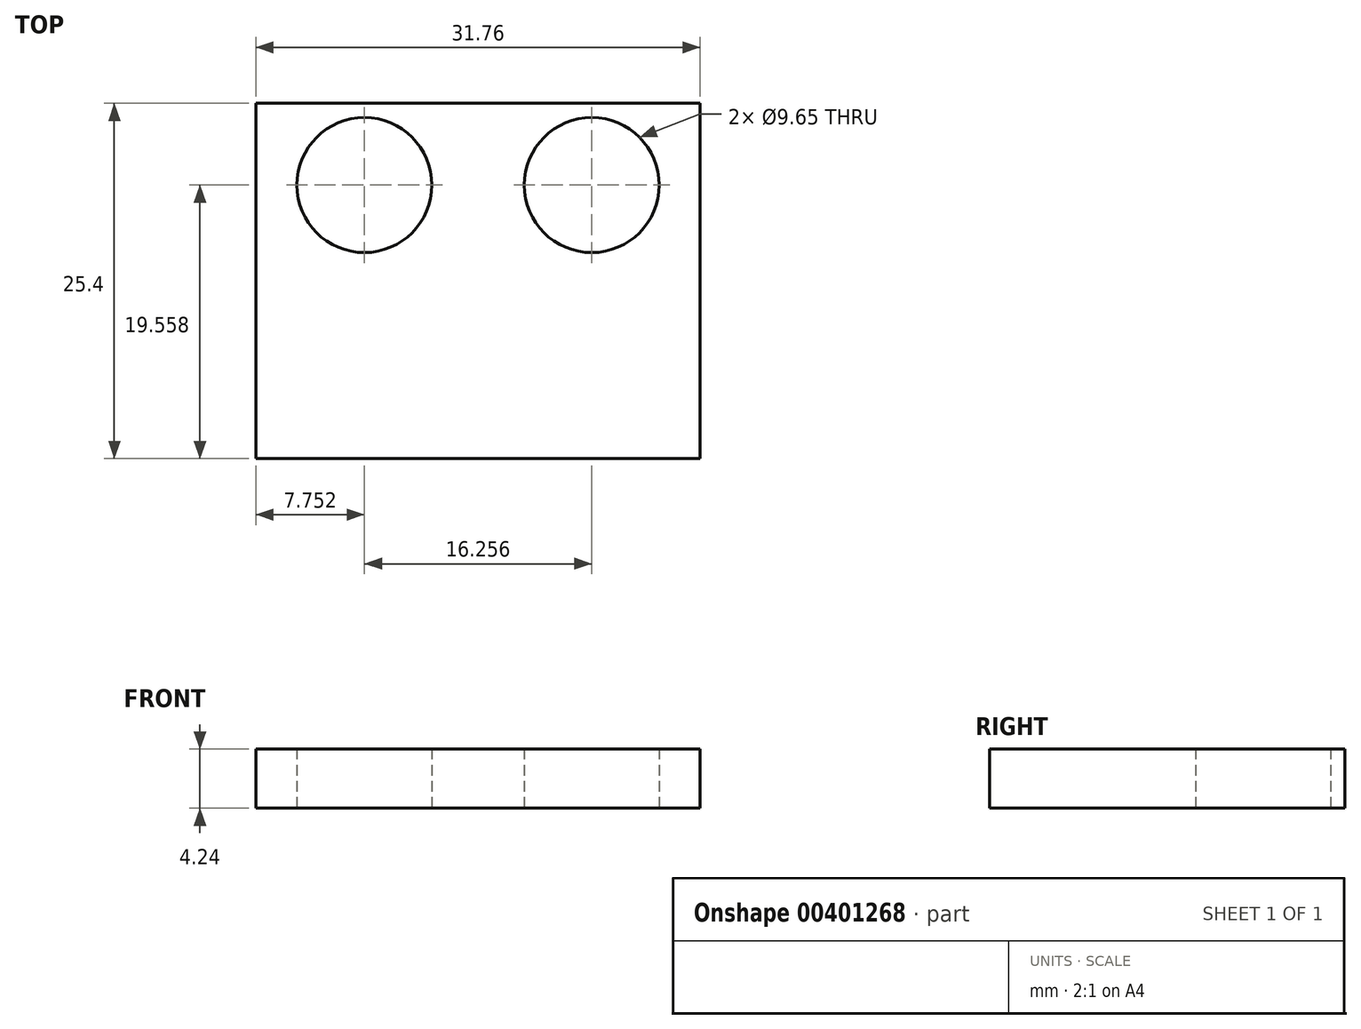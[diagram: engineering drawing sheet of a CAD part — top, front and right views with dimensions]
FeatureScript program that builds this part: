
annotation { "Feature Type Name" : "Feature", "Feature Type Description" : "" }
export const myFeature = defineFeature(function(context is Context, id is Id, definition is map)
    precondition{}
    {
        {
            var Q0;
            Q0=qCreatedBy(makeId("Top.planeOp"),FACE);
            var sketch = newSketch(context, id + "F0", { "sketchPlane" : qUnion([Q0])});
            skLineSegment(sketch, "E0.bottom", {"start": v(-15.87, -12.7) * mm, "end": v(15.88, -12.7) * mm});
            skLineSegment(sketch, "E0.top", {"start": v(-15.88, 12.7) * mm, "end": v(15.88, 12.7) * mm});
            skLineSegment(sketch, "E0.left", {"start": v(-15.87, -12.7) * mm, "end": v(-15.88, 12.7) * mm});
            skLineSegment(sketch, "E0.right", {"start": v(15.88, -12.7) * mm, "end": v(15.87, 12.7) * mm});
            skPoint(sketch, "E0.middle", {"position": v(0, 0) * mm});
            skCircle(sketch, "E1", {"center": v(-8.13, 6.86) * mm, "radius": 4.83 * mm});
            skCircle(sketch, "E2", {"center": v(8.13, 6.86) * mm, "radius": 4.83 * mm});
            skSolve(sketch);
        }
        {
            var Q0;
            Q0 = qSketchRegion(id + "F0", true);
            extrude(context, id + "F1", {"entities" : qUnion([Q0]), "depth" : 4.24 * mm});
        }
    });
